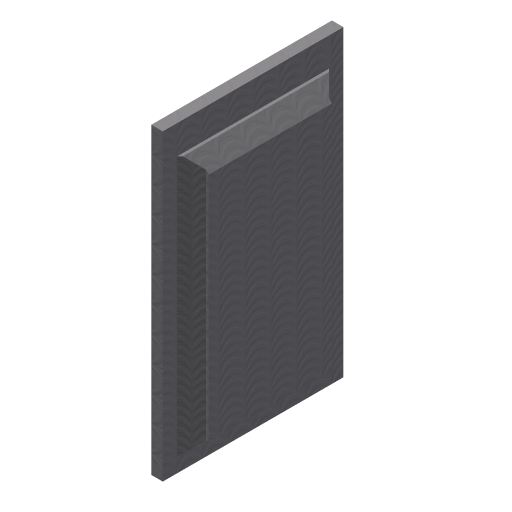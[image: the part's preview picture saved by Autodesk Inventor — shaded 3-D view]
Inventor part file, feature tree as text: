
AUTODESK INVENTOR PART (.ipt)
format: ipt  version: 2024 (Build 280153000, 153)  size: 196,096 bytes
history: native  units: mm
features: extrude x3, sketch x2, chamfer x1, projected_geometry x1
ambient origin geometry x8: Origin, YZ Plane, XZ Plane, XY Plane, X Axis, Y Axis, Z Axis, Center Point
bodies: Solid1 (feature_tree)
feature tree (7):
  sketch  "Sketch1"  dims[d0=487.0mm d1=274.0mm]
  extrude  "Extrusion1"  Depth=274.0mm
  extrude  "Extrusion2"  Depth=20.0mm TaperAngle=0.0deg
  extrude  "Extrusion3"  Depth=2.0mm TaperAngle=0.0deg
  chamfer  "Chamfer1"  Distance=50.0mm
  sketch  "Sketch2"  dims[d2=20.0mm d3=20.0mm d4=0.0mm d5=2.0mm d6=0.0mm d7=50.0mm d8=30.0mm d9=0.0mm d10=25.0mm d11=2.0mm d12=45.0deg]
  projected_geometry  "Projected Loop1"
